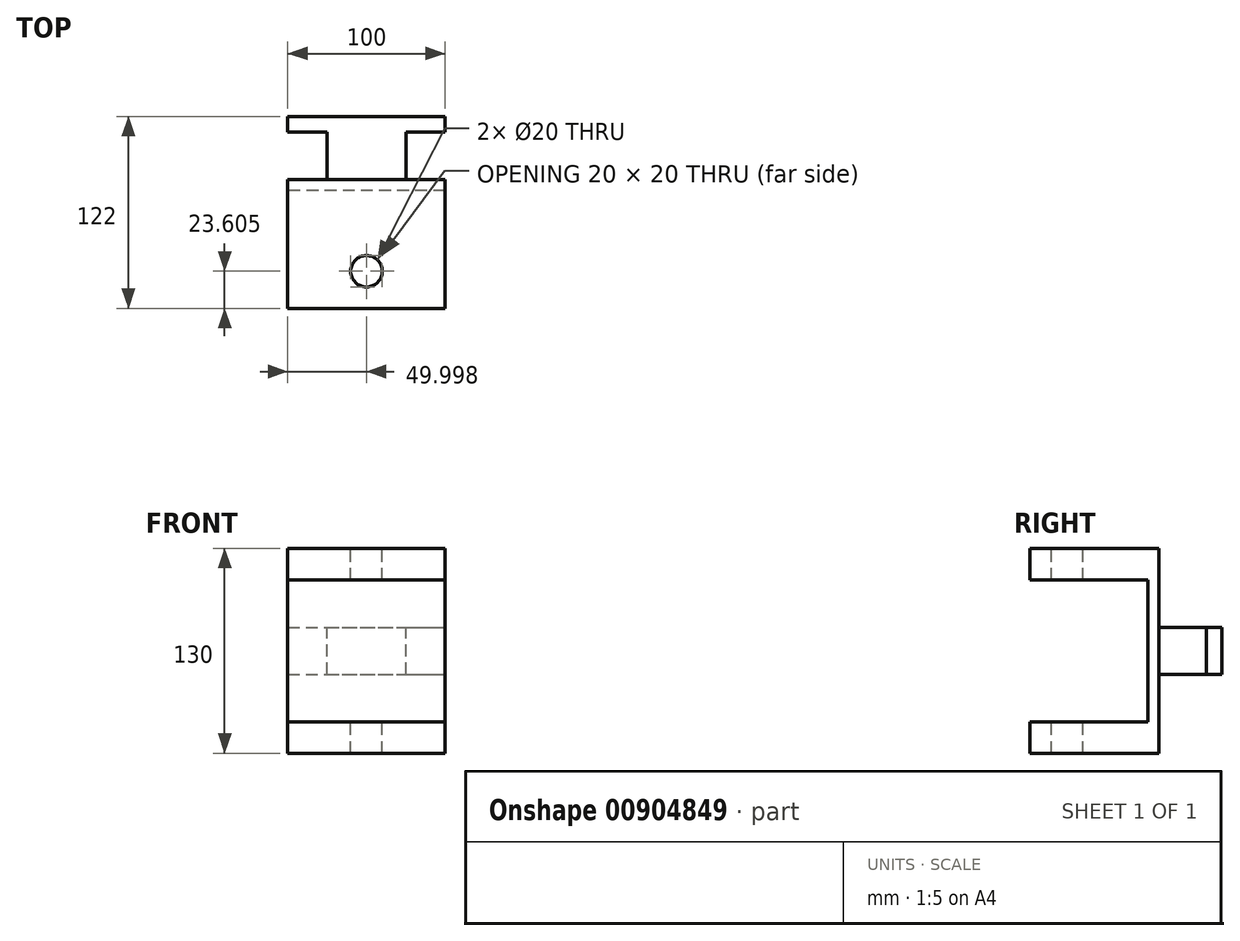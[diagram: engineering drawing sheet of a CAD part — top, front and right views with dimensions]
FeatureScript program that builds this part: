
annotation { "Feature Type Name" : "Feature", "Feature Type Description" : "" }
export const myFeature = defineFeature(function(context is Context, id is Id, definition is map)
    precondition{}
    {
        {
            var Q0;
            Q0=qCreatedBy(makeId("Front.planeOp"),FACE);
            var sketch = newSketch(context, id + "F0", { "sketchPlane" : qUnion([Q0])});
            skLineSegment(sketch, "E0.bottom", {"start": v(-33.85, 16.14) * mm, "end": v(66.15, 16.14) * mm});
            skLineSegment(sketch, "E0.top", {"start": v(-33.85, -13.86) * mm, "end": v(66.15, -13.86) * mm});
            skLineSegment(sketch, "E0.left", {"start": v(-33.85, 16.14) * mm, "end": v(-33.85, -13.86) * mm});
            skLineSegment(sketch, "E0.right", {"start": v(66.15, 16.14) * mm, "end": v(66.15, -13.86) * mm});
            skSolve(sketch);
        }
        {
            var Q0;
            Q0=makeQuery(id+"F0.imprint","IMPRINT",FACE,{"disambiguationData":[TD([[makeQuery(id+"F0.imprint","IMPRINT",EDGE,{"derivedFrom":sQuery(id+"F0.wireOp",EDGE,"E0.bottom")}),-1.0]])]});
            extrude(context, id + "F1", {"entities" : qUnion([Q0]), "depth" : 10 * mm, "offsetDistance" : 25 * mm});
        }
        {
            var Q0;
            Q0=makeQuery(id+"F1.opExtrude","CAP_FACE",FACE,{"disambiguationData":[OSD([sQuery(id+"F0.wireOp",EDGE,"E0.bottom"),sQuery(id+"F0.wireOp",EDGE,"E0.top"),sQuery(id+"F0.wireOp",EDGE,"E0.left"),sQuery(id+"F0.wireOp",EDGE,"E0.right")])],"isStart":false});
            var sketch = newSketch(context, id + "F2", { "sketchPlane" : qUnion([Q0])});
            skLineSegment(sketch, "E1.bottom", {"start": v(-8.85, -13.86) * mm, "end": v(41.15, -13.86) * mm});
            skLineSegment(sketch, "E1.top", {"start": v(-8.85, 16.14) * mm, "end": v(41.15, 16.14) * mm});
            skLineSegment(sketch, "E1.left", {"start": v(-8.85, -13.86) * mm, "end": v(-8.85, 16.14) * mm});
            skLineSegment(sketch, "E1.right", {"start": v(41.15, -13.86) * mm, "end": v(41.15, 16.14) * mm});
            skSolve(sketch);
        }
        {
            var Q0;
            Q0 = qSketchRegion(id + "F2", true);
            var Q1;
            Q1=makeQuery(id+"F2.imprint","IMPRINT",FACE,{"disambiguationData":[TD([[makeQuery(id+"F2.imprint","IMPRINT",EDGE,{"derivedFrom":sQuery(id+"F2.wireOp",EDGE,"E1.bottom")}),1.0]])]});
            extrude(context, id + "F3", {"entities" : qUnion([Q0, Q1]), "operationType" : NewBodyOperationType.ADD, "depth" : 30 * mm, "offsetDistance" : 25 * mm});
        }
        {
            var Q0;
            Q0=makeQuery(id+"F3.opExtrude","CAP_FACE",FACE,{"disambiguationData":[OSD([sQuery(id+"F2.wireOp",EDGE,"E1.bottom"),sQuery(id+"F2.wireOp",EDGE,"E1.top"),sQuery(id+"F2.wireOp",EDGE,"E1.left"),sQuery(id+"F2.wireOp",EDGE,"E1.right")])],"isStart":false});
            var sketch = newSketch(context, id + "F4", { "sketchPlane" : qUnion([Q0])});
            skLineSegment(sketch, "E2.bottom", {"start": v(-33.85, -63.86) * mm, "end": v(66.15, -63.86) * mm});
            skLineSegment(sketch, "E2.top", {"start": v(-33.85, 66.14) * mm, "end": v(66.15, 66.14) * mm});
            skLineSegment(sketch, "E2.left", {"start": v(-33.85, -63.86) * mm, "end": v(-33.85, 66.14) * mm});
            skLineSegment(sketch, "E2.right", {"start": v(66.15, -63.86) * mm, "end": v(66.15, 66.14) * mm});
            skSolve(sketch);
        }
        {
            var Q0;
            Q0=makeQuery(id+"F4.imprint","IMPRINT",FACE,{"disambiguationData":[TD([[makeQuery(id+"F4.imprint","IMPRINT",EDGE,{"derivedFrom":sQuery(id+"F4.wireOp",EDGE,"E2.bottom")}),1.0]])]});
            var Q1;
            Q1=makeQuery(id+"F4.imprint","IMPRINT",FACE,{"disambiguationData":[TD([[makeQuery(id+"F4.imprint","IMPRINT",EDGE,{"derivedFrom":makeQuery(id+"F3.opExtrude","CAP_EDGE",EDGE,{"disambiguationData":[OSD([sQuery(id+"F2.wireOp",EDGE,"E1.bottom")])],"isStart":false})}),1.0]])]});
            extrude(context, id + "F5", {"entities" : qUnion([Q0, Q1]), "operationType" : NewBodyOperationType.ADD, "depth" : 7 * mm, "offsetDistance" : 25 * mm});
        }
        {
            var Q0;
            Q0=makeQuery(id+"F5.opExtrude","CAP_FACE",FACE,{"disambiguationData":[OSD([sQuery(id+"F4.wireOp",EDGE,"E2.bottom"),sQuery(id+"F4.wireOp",EDGE,"E2.top"),sQuery(id+"F4.wireOp",EDGE,"E2.left"),sQuery(id+"F4.wireOp",EDGE,"E2.right")])],"isStart":false});
            var sketch = newSketch(context, id + "F6", { "sketchPlane" : qUnion([Q0])});
            skLineSegment(sketch, "E3.bottom", {"start": v(66.15, -63.86) * mm, "end": v(-33.85, -63.86) * mm});
            skLineSegment(sketch, "E3.top", {"start": v(66.15, -43.86) * mm, "end": v(-33.85, -43.86) * mm});
            skLineSegment(sketch, "E3.left", {"start": v(66.15, -63.86) * mm, "end": v(66.15, -43.86) * mm});
            skLineSegment(sketch, "E3.right", {"start": v(-33.85, -63.86) * mm, "end": v(-33.85, -43.86) * mm});
            skLineSegment(sketch, "E4.bottom", {"start": v(66.15, 66.14) * mm, "end": v(-33.85, 66.14) * mm});
            skLineSegment(sketch, "E4.top", {"start": v(66.15, 46.14) * mm, "end": v(-33.85, 46.14) * mm});
            skLineSegment(sketch, "E4.left", {"start": v(66.15, 66.14) * mm, "end": v(66.15, 46.14) * mm});
            skLineSegment(sketch, "E4.right", {"start": v(-33.85, 66.14) * mm, "end": v(-33.85, 46.14) * mm});
            skSolve(sketch);
        }
        {
            var Q0;
            Q0=makeQuery(id+"F6.imprint","IMPRINT",FACE,{"disambiguationData":[TD([[makeQuery(id+"F6.imprint","IMPRINT",EDGE,{"derivedFrom":sQuery(id+"F6.wireOp",EDGE,"E3.bottom")}),1.0]])]});
            var Q1;
            Q1=makeQuery(id+"F6.imprint","IMPRINT",FACE,{"disambiguationData":[TD([[makeQuery(id+"F6.imprint","IMPRINT",EDGE,{"derivedFrom":sQuery(id+"F6.wireOp",EDGE,"E4.bottom")}),-1.0]])]});
            extrude(context, id + "F7", {"entities" : qUnion([Q0, Q1]), "operationType" : NewBodyOperationType.ADD, "depth" : 75 * mm, "offsetDistance" : 25 * mm});
        }
        {
            var Q0;
            Q0=makeQuery(id+"F7.boolean.opBoolean","MERGE",FACE,{"derivedFrom":[makeQuery(id+"F5.opExtrude","SWEPT_FACE",FACE,{"disambiguationData":[OSD([sQuery(id+"F4.wireOp",EDGE,"E2.top")])]}),makeQuery(id+"F7.opExtrude","SWEPT_FACE",FACE,{"disambiguationData":[OSD([sQuery(id+"F6.wireOp",EDGE,"E4.bottom")])]})]});
            var sketch = newSketch(context, id + "F8", { "sketchPlane" : qUnion([Q0])});
            skPoint(sketch, "E5.positionSnap0", {"position": v(66.15, -81) * mm});
            skPoint(sketch, "E6", {"position": v(16.15, -40) * mm});
            skPoint(sketch, "E7", {"position": v(16.15, -98.4) * mm});
            skCircle(sketch, "E8", {"center": v(16.15, -98.4) * mm, "radius": 10 * mm});
            skSolve(sketch);
        }
        {
            var Q0;
            Q0=makeQuery(id+"F8.imprint","IMPRINT",FACE,{"disambiguationData":[TD([[makeQuery(id+"F8.imprint","IMPRINT",EDGE,{"derivedFrom":sQuery(id+"F8.wireOp",EDGE,"E8")}),1.0]])]});
            extrude(context, id + "F9", {"entities" : qUnion([Q0]), "operationType" : NewBodyOperationType.REMOVE, "endBound" : BoundingType.THROUGH_ALL, "oppositeDirection" : true, "depth" : 25 * mm, "offsetDistance" : 25 * mm});
        }
    });
